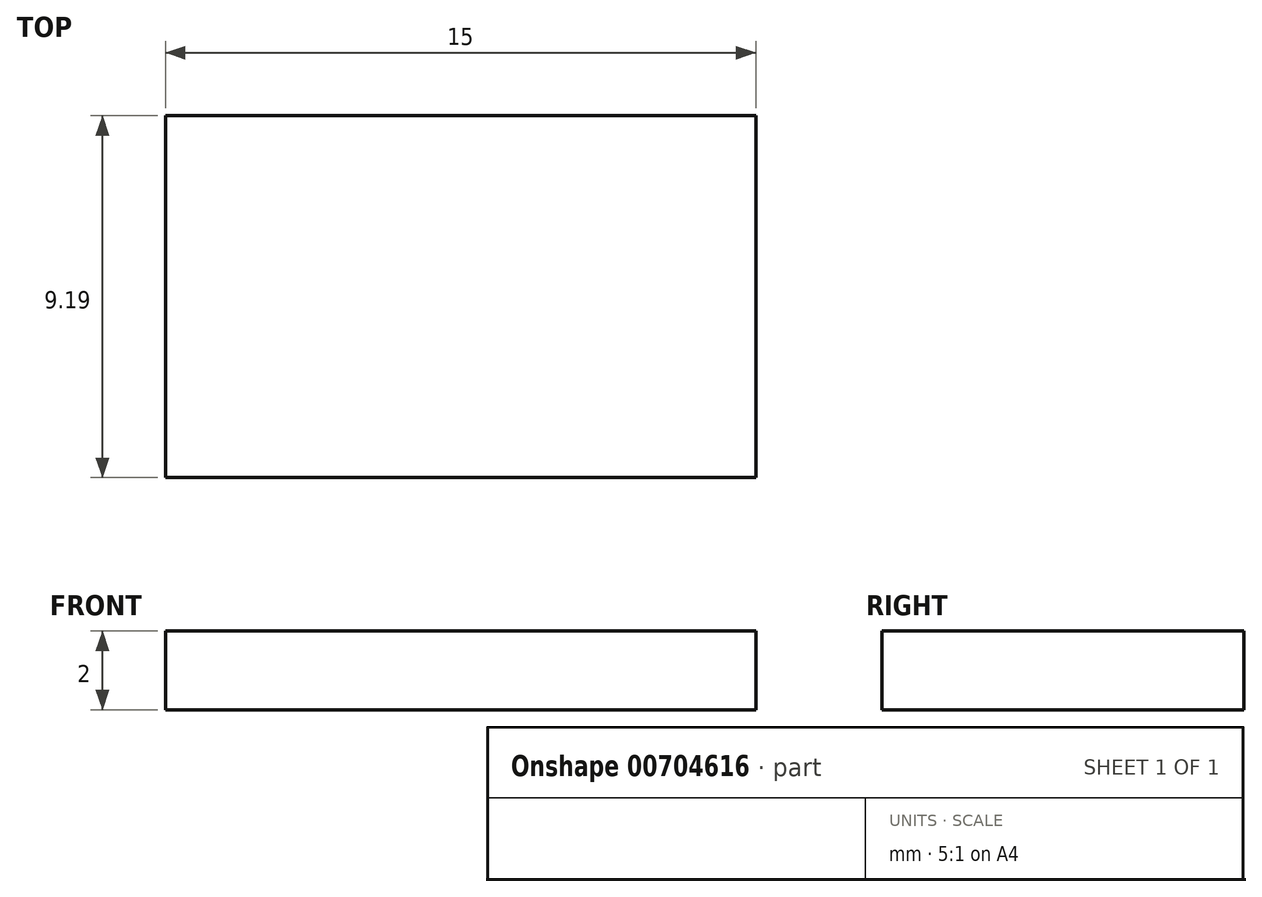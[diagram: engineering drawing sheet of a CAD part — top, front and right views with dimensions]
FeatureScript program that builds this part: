
annotation { "Feature Type Name" : "Feature", "Feature Type Description" : "" }
export const myFeature = defineFeature(function(context is Context, id is Id, definition is map)
    precondition{}
    {
        {
            var Q0;
            Q0=qCreatedBy(makeId("Top.planeOp"),FACE);
            var sketch = newSketch(context, id + "F0", { "sketchPlane" : qUnion([Q0])});
            skLineSegment(sketch, "E0.bottom", {"start": v(-7.88, -0.67) * mm, "end": v(7.12, -0.67) * mm});
            skLineSegment(sketch, "E0.top", {"start": v(-7.88, -9.86) * mm, "end": v(7.12, -9.86) * mm});
            skLineSegment(sketch, "E0.left", {"start": v(-7.88, -0.67) * mm, "end": v(-7.88, -9.86) * mm});
            skLineSegment(sketch, "E0.right", {"start": v(7.12, -0.67) * mm, "end": v(7.12, -9.86) * mm});
            skSolve(sketch);
        }
        {
            var Q0;
            Q0 = qSketchRegion(id + "F0", true);
            extrude(context, id + "F1", {"entities" : qUnion([Q0]), "depth" : 2 * mm, "offsetDistance" : 25 * mm});
        }
    });
